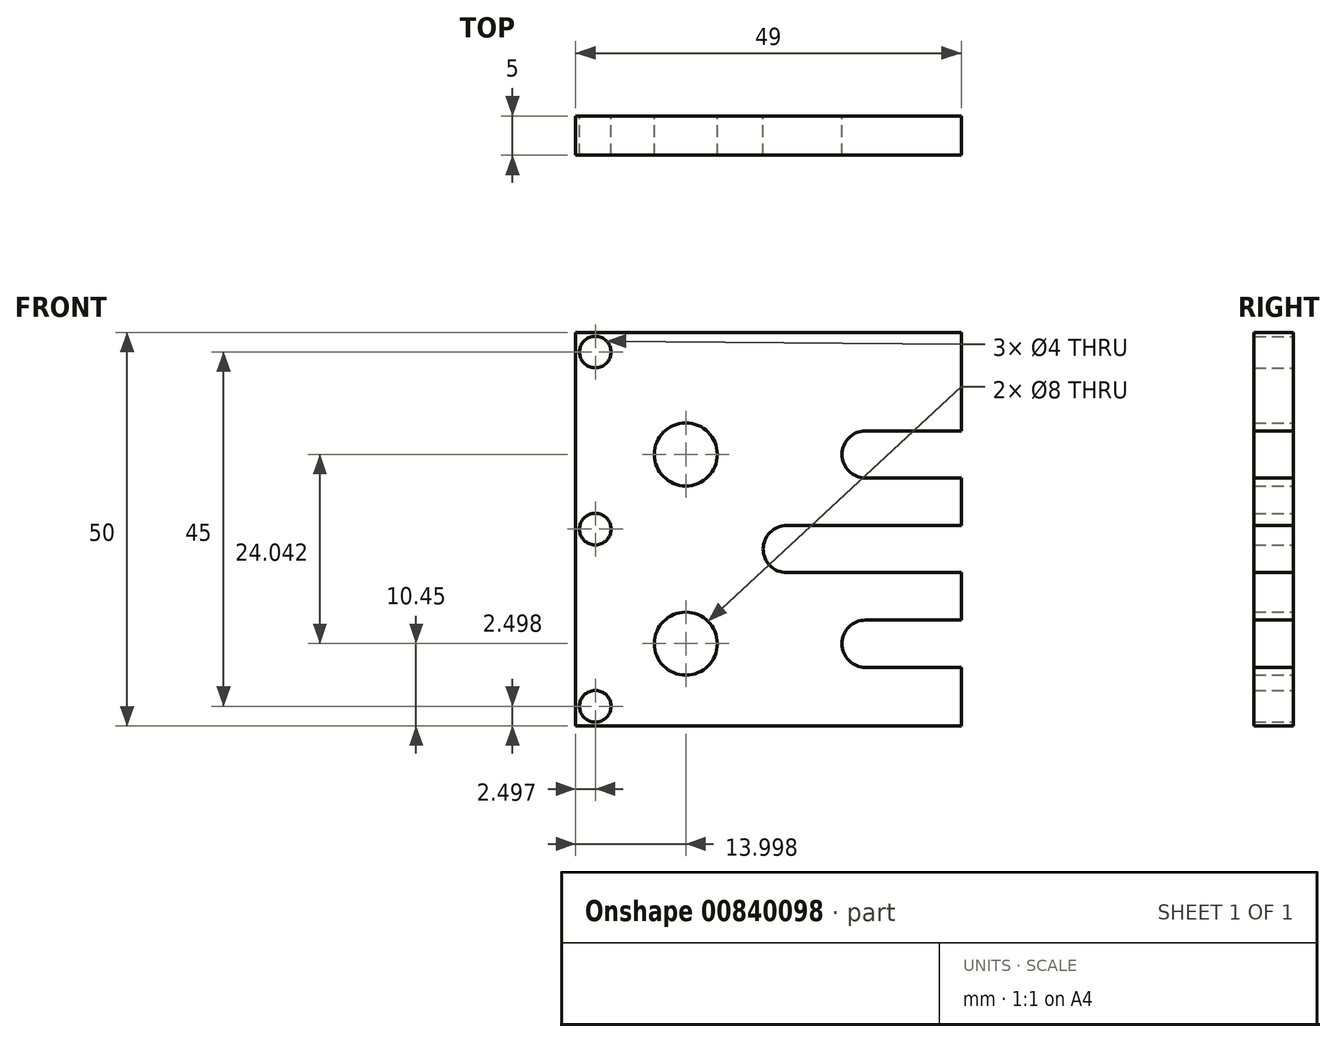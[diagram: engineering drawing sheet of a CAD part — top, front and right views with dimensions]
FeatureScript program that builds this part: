
annotation { "Feature Type Name" : "Feature", "Feature Type Description" : "" }
export const myFeature = defineFeature(function(context is Context, id is Id, definition is map)
    precondition{}
    {
        {
            var Q0;
            Q0=qCreatedBy(makeId("Front.planeOp"),FACE);
            var sketch = newSketch(context, id + "F0", { "sketchPlane" : qUnion([Q0])});
            skPoint(sketch, "E0", {"position": v(-44.07, 1.1) * mm});
            skLineSegment(sketch, "E1", {"start": v(-9.07, 40.66) * mm, "end": v(-9.07, 28.15) * mm});
            skPoint(sketch, "E2", {"position": v(-31.24, 13.14) * mm});
            skArc(sketch, "E3", {"start": v(-31.24, 16.14) * mm, "mid": v(-34.24, 13.14) * mm, "end": v(-31.24, 10.14) * mm});
            skLineSegment(sketch, "E4.right", {"start": v(-58.07, -9.34) * mm, "end": v(-58.07, 40.66) * mm});
            skPoint(sketch, "E5", {"position": v(-21.25, 25.15) * mm});
            skPoint(sketch, "E6", {"position": v(-21.25, 1.1) * mm});
            skArc(sketch, "E7", {"start": v(-21.25, 28.15) * mm, "mid": v(-24.25, 25.14) * mm, "end": v(-21.25, 22.15) * mm});
            skArc(sketch, "E8", {"start": v(-21.25, 4.1) * mm, "mid": v(-24.25, 1.1) * mm, "end": v(-21.25, -1.9) * mm});
            skCircle(sketch, "E9", {"center": v(-44.07, 25.15) * mm, "radius": 4 * mm});
            skCircle(sketch, "E10", {"center": v(-44.07, 1.1) * mm, "radius": 4 * mm});
            skLineSegment(sketch, "E11", {"start": v(-31.24, 16.14) * mm, "end": v(-9.07, 16.14) * mm});
            skLineSegment(sketch, "E12", {"start": v(-31.24, 10.14) * mm, "end": v(-9.07, 10.14) * mm});
            skLineSegment(sketch, "E13", {"start": v(-21.25, 28.15) * mm, "end": v(-9.07, 28.15) * mm});
            skLineSegment(sketch, "E14", {"start": v(-21.25, 22.15) * mm, "end": v(-9.07, 22.15) * mm});
            skLineSegment(sketch, "E15", {"start": v(-9.08, 4.1) * mm, "end": v(-9.07, 4.1) * mm});
            skLineSegment(sketch, "E16", {"start": v(-21.25, -1.9) * mm, "end": v(-9.07, -1.9) * mm});
            skLineSegment(sketch, "E17", {"start": v(-21.25, 4.1) * mm, "end": v(-9.07, 4.1) * mm});
            skLineSegment(sketch, "E18", {"start": v(-58.07, 40.66) * mm, "end": v(-9.07, 40.66) * mm});
            skLineSegment(sketch, "E19", {"start": v(-9.07, 22.15) * mm, "end": v(-9.07, 16.14) * mm});
            skLineSegment(sketch, "E20", {"start": v(-9.07, 10.14) * mm, "end": v(-9.07, 4.1) * mm});
            skLineSegment(sketch, "E21", {"start": v(-9.07, -1.9) * mm, "end": v(-9.07, -9.34) * mm});
            skLineSegment(sketch, "E22", {"start": v(-58.07, -9.34) * mm, "end": v(-9.07, -9.34) * mm});
            skPoint(sketch, "E23", {"position": v(-55.57, -6.84) * mm});
            skPoint(sketch, "E24", {"position": v(-55.57, 38.16) * mm});
            skPoint(sketch, "E25", {"position": v(-55.57, 15.66) * mm});
            skCircle(sketch, "E26", {"center": v(-55.57, 38.16) * mm, "radius": 2 * mm});
            skCircle(sketch, "E27", {"center": v(-55.57, 15.66) * mm, "radius": 2 * mm});
            skCircle(sketch, "E28", {"center": v(-55.57, -6.84) * mm, "radius": 2 * mm});
            skSolve(sketch);
        }
        {
            var Q0;
            Q0 = qSketchRegion(id + "F0", true);
            extrude(context, id + "F1", {"entities" : qUnion([Q0]), "depth" : 5 * mm, "offsetDistance" : 25 * mm});
        }
    });
